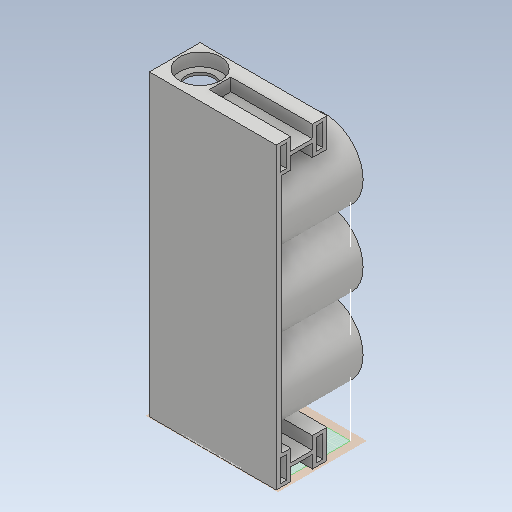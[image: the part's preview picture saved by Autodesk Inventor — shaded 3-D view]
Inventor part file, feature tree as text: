
AUTODESK INVENTOR PART (.ipt)
format: ipt  version: 2020 (Build 240168000, 168)  size: 855,040 bytes
history: native  units: mm
features: sketch x31, extrude x28, fillet x6
ambient origin geometry x8: Origin, YZ Plane, XZ Plane, XY Plane, X Axis, Y Axis, Z Axis, Center Point
bodies: Solid1 (feature_tree)
feature tree (65):
  extrude  "Extrusion1"  Depth=165.0mm
  extrude  "Extrusion2"  Depth=3.0mm
  extrude  "Extrusion3"  Depth=25.0mm TaperAngle=0.0deg
  extrude  "Extrusion4"  Depth=25.0mm
  extrude  "Extrusion5"  Depth=15.5mm
  extrude  "Extrusion6"  Depth=5.0mm TaperAngle=0.0deg
  fillet  "Fillet1"  Radius=5.0mm
  extrude  "Extrusion7"  Depth=10.0mm TaperAngle=0.0deg
  fillet  "Fillet2"  Radius=2.0mm
  extrude  "Extrusion8"  Depth=8.0mm
  extrude  "Extrusion9"  Depth=16.0mm
  fillet  "Fillet3"  Radius=8.0mm
  extrude  "Extrusion10"  Depth=6.0mm
  extrude  "Extrusion11"  Depth=3.5mm
  sketch  "Sketch12"  dims[d32=12.25mm d33=3.5mm]
  sketch  "Sketch13"  dims[d34=12.25mm d35=12.25mm]
  extrude  "Extrusion12"  Depth=3.5mm
  extrude  "Extrusion13"  Depth=12.25mm
  sketch  "Sketch16"  dims[d41=8.0mm d42=1.0mm]
  extrude  "Extrusion14"  Depth=40.0mm TaperAngle=0.0deg
  extrude  "Extrusion15"  Depth=1.0mm
  extrude  "Extrusion16"  Depth=1.0mm
  extrude  "Extrusion17"  Depth=12.0mm TaperAngle=0.0deg
  extrude  "Extrusion18"  Depth=3.0mm TaperAngle=0.0deg
  fillet  "Fillet4"  Radius=3.0mm
  extrude  "Extrusion19"  Depth=38.75mm
  extrude  "Extrusion20"  Depth=38.75mm
  extrude  "Extrusion21"  Depth=38.75mm
  extrude  "Extrusion22"  Depth=2.0mm
  extrude  "Extrusion23"  Depth=2.0mm
  extrude  "Extrusion24"  Depth=10.0mm TaperAngle=0.0deg
  fillet  "Fillet5"  Radius=10.0mm
  extrude  "Extrusion25"  Depth=2.0mm TaperAngle=0.0deg
  fillet  "Fillet6"  Radius=2.0mm
  extrude  "Extrusion26"  Depth=2.0mm
  extrude  "Extrusion27"  Depth=5.0mm
  extrude  "Extrusion28"  Depth=7.0mm TaperAngle=0.0deg
  sketch  "Sketch1"  dims[d0=25.0mm d1=165.0mm]
  sketch  "Sketch2"  dims[d2=3.0mm d3=0.0mm d4=8.5mm]
  sketch  "Sketch3"  dims[d5=8.5mm d6=25.0mm d7=0.0mm]
  sketch  "Sketch4"  dims[d8=25.0mm d9=22.75mm]
  sketch  "Sketch5"  dims[d10=7.1mm d11=0.0mm d12=15.5mm]
  sketch  "Sketch6"  dims[d13=165.0mm d14=0.0mm d15=7.1mm d16=0.0mm d17=5.0mm]
  sketch  "Sketch7"  dims[d18=5.0mm d19=10.0mm d20=0.0mm d21=2.0mm]
  sketch  "Sketch8"  dims[d22=16.0mm d23=8.0mm]
  sketch  "Sketch9"  dims[d24=16.0mm d25=16.0mm d26=8.0mm]
  sketch  "Sketch10"  dims[d27=45.0mm d28=0.0mm d29=6.0mm]
  sketch  "Sketch11"  dims[d30=12.25mm d31=3.5mm]
  sketch  "Sketch14"  dims[d36=3.5mm d37=40.0mm d38=0.0mm]
  sketch  "Sketch15"  dims[d39=1.0mm d40=2.0mm]
  sketch  "Sketch17"  dims[d43=2.0mm d44=12.0mm d45=0.0mm]
  sketch  "Sketch18"  dims[d46=6.0mm d47=7.1mm d48=0.0mm d49=3.0mm d50=0.0mm]
  sketch  "Sketch19"  dims[d51=42.0mm d52=38.75mm]
  sketch  "Sketch20"  dims[d53=42.0mm d54=38.75mm]
  sketch  "Sketch21"  dims[d55=42.0mm d56=38.75mm]
  sketch  "Sketch22"  dims[d57=45.0mm d58=0.0mm d59=2.0mm]
  sketch  "Sketch23"  dims[d60=4.0mm d61=2.0mm]
  sketch  "Sketch24"  dims[d62=4.0mm d63=45.0mm d64=0.0mm d65=10.0mm]
  sketch  "Sketch25"  dims[d66=12.0mm d67=0.0mm d68=2.0mm d69=0.0mm d70=2.0mm d71=0.0mm]
  sketch  "Sketch26"  dims[d72=2.0mm d73=2.0mm]
  sketch  "Sketch27"  dims[d74=5.0mm d75=0.0mm d76=2.0mm]
  sketch  "Sketch28"  dims[d77=2.0mm d78=7.0mm d79=0.0mm]
  sketch  "Sketch29"  dims[d80=1.0mm]
  sketch  "Sketch30"  dims[d81=0.25mm]
  sketch  "Sketch31"  dims[d82=0.25mm d83=44.75mm d84=0.0mm d85=44.0mm d86=0.0mm d87=22.6mm d88=8.5mm d89=0.0mm d90=22.6mm d91=8.5mm d92=0.0mm d93=27.0mm d94=0.0mm d95=60.0mm d96=19.05mm d97=3.0mm d98=0.0mm d99=31.75mm d100=19.05mm d101=19.05mm d102=31.5mm d103=0.0mm d104=38.0mm d105=12.954mm d106=27.5mm d107=0.0mm d108=18.0mm d109=18.0mm d110=18.0mm d111=18.0mm d112=18.0mm d113=0.0mm d114=2.0mm d115=2.0mm d116=2.0mm d117=5.0mm d118=0.0mm]
